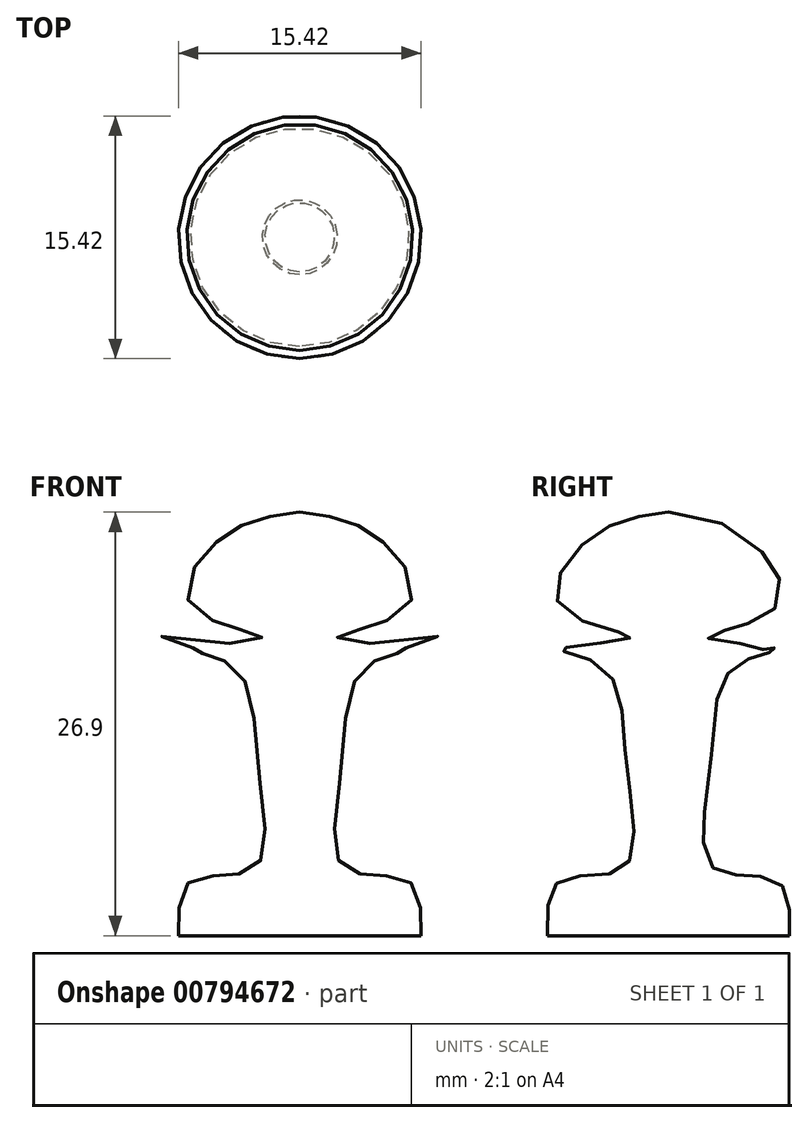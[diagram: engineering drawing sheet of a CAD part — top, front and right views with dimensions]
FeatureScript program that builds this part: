
annotation { "Feature Type Name" : "Feature", "Feature Type Description" : "" }
export const myFeature = defineFeature(function(context is Context, id is Id, definition is map)
    precondition{}
    {
        {
            var Q0;
            Q0=qCreatedBy(makeId("Top.planeOp"),FACE);
            var sketch = newSketch(context, id + "F0", { "sketchPlane" : qUnion([Q0])});
            skCircle(sketch, "E0", {"center": v(0, 0) * mm, "radius": 7.73 * mm});
            skSolve(sketch);
        }
        {
            var Q0;
            Q0=qCreatedBy(makeId("Right.planeOp"),FACE);
            var sketch = newSketch(context, id + "F1", { "sketchPlane" : qUnion([Q0])});
            skFitSpline(sketch, "E1", {"points": [v(7.7, 0) * mm, v(6.85, 3.5) * mm, v(2.84, 4.3) * mm, v(2.67, 10.95) * mm, v(4.37, 17.2) * mm, v(6.9, 18.22) * mm, v(2.4, 18.95) * mm, v(6.79, 20.81) * mm, v(4.99, 25.26) * mm, v(0, 26.9) * mm], "startDerivative": vector(1.32, 45.8) * mm, "endDerivative": vector(-43.55, 5.39) * mm});
            skLineSegment(sketch, "E2", {"start": v(0, 26.9) * mm, "end": v(0, 0) * mm});
            skLineSegment(sketch, "E3", {"start": v(7.7, 0) * mm, "end": v(0, 0) * mm});
            skSolve(sketch);
        }
        {
            var Q0;
            Q0=makeQuery(id+"F1.imprint","IMPRINT",FACE,{"disambiguationData":[TD([[makeQuery(id+"F1.imprint","IMPRINT",EDGE,{"derivedFrom":sQuery(id+"F1.wireOp",EDGE,"E1")}),1.0]])]});
            var Q1;
            Q1=sQuery(id+"F0.wireOp",EDGE,"E0");
            sweep(context, id + "F2", {"profiles" : qUnion([Q0]), "path" : qUnion([Q1])});
        }
    });
